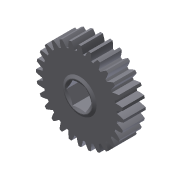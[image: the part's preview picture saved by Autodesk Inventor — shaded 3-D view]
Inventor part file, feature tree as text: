
AUTODESK INVENTOR PART (.ipt)
format: ipt  version: 2013 (Build 170138000, 138)  size: 273,408 bytes
history: native  units: mm (DEFAULTED — no unit token found)
features: sketch x5, extrude x3, plane x3, other x3, chamfer x1, revolve x1, projected_geometry x1
ambient origin geometry x8: Origin, YZ Plane, XZ Plane, XY Plane, X Axis, Y Axis, Z Axis, Center Point
bodies: Solid1 (feature_tree)
feature tree (17):
  extrude  "Extrusion1"  Depth=9.525mm TaperAngle=0.0deg
  plane  "Work Plane1"
  plane  "Work Plane2"
  plane  "Work Plane3"
  other  "Spur Gear"
  extrude  "Extrusion2"  Depth=76.2mm TaperAngle=0.0deg
  extrude  "Extrusion3"  TaperAngle=0.0deg  [1 undecoded]
  chamfer  "Chamfer1"  Distance=0.635mm
  revolve  "Revolution1"  [1 undecoded]
  sketch  "Sketch1"  dims[d0=38.2016mm d1=9.525mm d2=0.0mm]
  sketch  "Sketch2"  dims[d3=35.56mm d4=76.2mm d5=0.0mm]
  other  "Srf1"
  sketch  "Sketch3"  dims[d6=0.0mm d7=1.121997mm d9=0.0mm]
  sketch  "Sketch4"  dims[d20=14.605mm d21=0.635mm d22=0.0mm]
  sketch  "Sketch5"  dims[d23=9.525mm d24=0.0mm d25=0.0mm d26=1.143mm d27=3.175mm d28=26.345745mm d30=1.143mm d31=90.0deg]
  other  "Pitch Diameter"
  projected_geometry  "Project Cut Edges1"
note: 2 required parameter values undecoded (feature->parameter linkage not recoverable at this tier; creation-order binding heuristic only, values carry confidence <= 0.55)